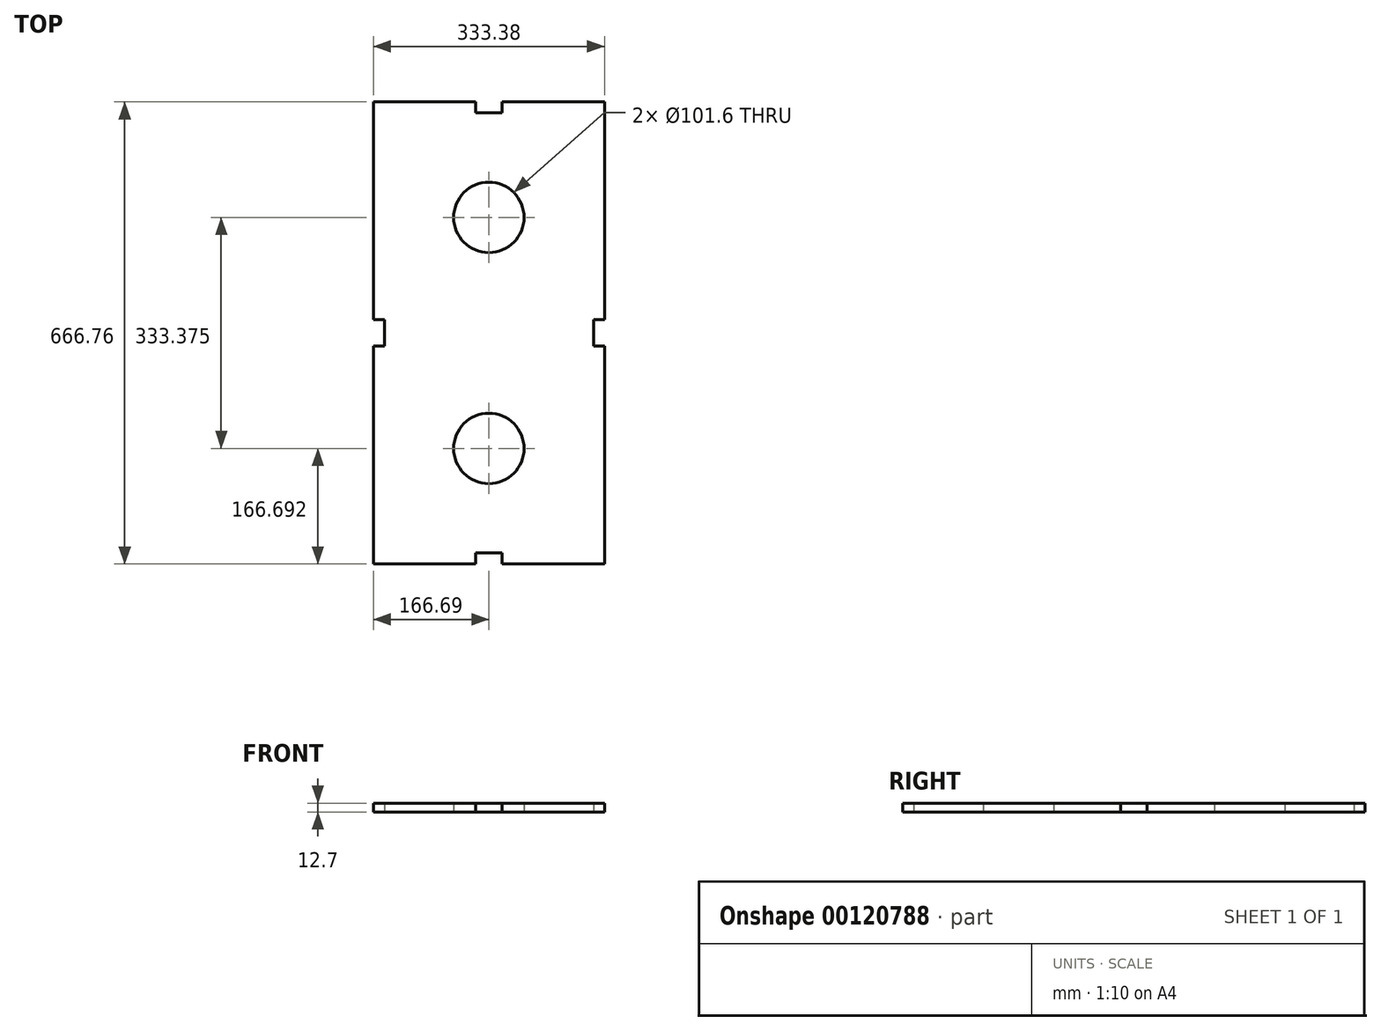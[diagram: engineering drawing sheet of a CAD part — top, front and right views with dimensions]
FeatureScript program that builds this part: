
annotation { "Feature Type Name" : "Feature", "Feature Type Description" : "" }
export const myFeature = defineFeature(function(context is Context, id is Id, definition is map)
    precondition{}
    {
        {
            var Q0;
            Q0=qCreatedBy(makeId("Top.planeOp"),FACE);
            var sketch = newSketch(context, id + "F0", { "sketchPlane" : qUnion([Q0])});
            skLineSegment(sketch, "E0.bottom", {"start": v(166.69, -166.69) * mm, "end": v(-166.69, -166.69) * mm});
            skLineSegment(sketch, "E0.top", {"start": v(166.69, 166.69) * mm, "end": v(-166.69, 166.69) * mm});
            skLineSegment(sketch, "E0.left", {"start": v(166.69, -166.69) * mm, "end": v(166.69, 166.69) * mm});
            skLineSegment(sketch, "E0.right", {"start": v(-166.69, -166.69) * mm, "end": v(-166.69, 166.69) * mm});
            skPoint(sketch, "E0.middle", {"position": v(0, 0) * mm});
            skCircle(sketch, "E1", {"center": v(0, -166.69) * mm, "radius": 50.8 * mm});
            skCircle(sketch, "E2", {"center": v(0, 166.69) * mm, "radius": 50.8 * mm});
            skLineSegment(sketch, "E3.bottom", {"start": v(-166.69, -19.05) * mm, "end": v(-150.81, -19.05) * mm});
            skLineSegment(sketch, "E3.top", {"start": v(-166.69, 19.05) * mm, "end": v(-150.81, 19.05) * mm});
            skLineSegment(sketch, "E3.left", {"start": v(-166.69, -19.05) * mm, "end": v(-166.69, 19.05) * mm});
            skLineSegment(sketch, "E3.right", {"start": v(-150.81, -19.05) * mm, "end": v(-150.81, 19.05) * mm});
            skPoint(sketch, "E3.middle", {"position": v(-158.75, 0) * mm});
            skPoint(sketch, "E3.middle.positionSnap0", {"position": v(-166.69, 0) * mm});
            skPoint(sketch, "E3.centerSnap0", {"position": v(-166.69, 0) * mm});
            skPoint(sketch, "E4.MirrorP", {"position": v(166.69, 0) * mm});
            skLineSegment(sketch, "E5.MirrorCS", {"start": v(166.69, -19.05) * mm, "end": v(150.81, -19.05) * mm});
            skPoint(sketch, "E6.MirrorP", {"position": v(158.75, 0) * mm});
            skLineSegment(sketch, "E7.MirrorCS", {"start": v(150.81, -19.05) * mm, "end": v(150.81, 19.05) * mm});
            skLineSegment(sketch, "E8.MirrorCS", {"start": v(166.69, -19.05) * mm, "end": v(166.69, 19.05) * mm});
            skLineSegment(sketch, "E9.MirrorCS", {"start": v(166.69, 19.05) * mm, "end": v(150.81, 19.05) * mm});
            skLineSegment(sketch, "E10.bottom", {"start": v(19.05, 333.38) * mm, "end": v(-19.05, 333.38) * mm});
            skLineSegment(sketch, "E10.top", {"start": v(19.05, 317.5) * mm, "end": v(-19.05, 317.5) * mm});
            skLineSegment(sketch, "E10.left", {"start": v(19.05, 333.38) * mm, "end": v(19.05, 317.5) * mm});
            skLineSegment(sketch, "E10.right", {"start": v(-19.05, 333.38) * mm, "end": v(-19.05, 317.5) * mm});
            skPoint(sketch, "E10.middle", {"position": v(0, 325.44) * mm});
            skLineSegment(sketch, "E11.MirrorCS", {"start": v(19.05, -333.38) * mm, "end": v(-19.05, -333.38) * mm});
            skLineSegment(sketch, "E12.MirrorCS", {"start": v(19.05, -333.38) * mm, "end": v(19.05, -317.5) * mm});
            skPoint(sketch, "E13.MirrorP", {"position": v(0, -325.44) * mm});
            skLineSegment(sketch, "E14.MirrorCS", {"start": v(-19.05, -333.38) * mm, "end": v(-19.05, -317.5) * mm});
            skLineSegment(sketch, "E15.MirrorCS", {"start": v(19.05, -317.5) * mm, "end": v(-19.05, -317.5) * mm});
            skLineSegment(sketch, "E16.bottom", {"start": v(-166.69, 333.38) * mm, "end": v(166.69, 333.38) * mm});
            skLineSegment(sketch, "E16.top", {"start": v(-166.69, -333.38) * mm, "end": v(166.69, -333.38) * mm});
            skLineSegment(sketch, "E16.left", {"start": v(-166.69, 333.38) * mm, "end": v(-166.69, -333.38) * mm});
            skLineSegment(sketch, "E16.right", {"start": v(166.69, 333.38) * mm, "end": v(166.69, -333.38) * mm});
            skSolve(sketch);
        }
        {
            var Q0;
            {var subQ1=sQuery(id+"F0.wireOp",EDGE,"E0.bottom");var subQ3=sQuery(id+"F0.wireOp",EDGE,"E1");var subQ4=makeQuery(id+"F0.imprint","INTERSECT",VERTEX,{"disambiguationData":[OD(0.0)],"derivedFrom":[subQ1,subQ3]});Q0=makeQuery(id+"F0.imprint","IMPRINT",FACE,{"disambiguationData":[TD([[makeQuery(id+"F0.imprint","IMPRINT",EDGE,{"disambiguationData":[TD([[subQ4,1.0]])],"derivedFrom":subQ3}),-1.0]])]});}
            var Q1;
            {var subQ1=sQuery(id+"F0.wireOp",EDGE,"E0.top");var subQ3=sQuery(id+"F0.wireOp",EDGE,"E2");var subQ4=makeQuery(id+"F0.imprint","INTERSECT",VERTEX,{"disambiguationData":[OD(0.0)],"derivedFrom":[subQ1,subQ3]});Q1=makeQuery(id+"F0.imprint","IMPRINT",FACE,{"disambiguationData":[TD([[makeQuery(id+"F0.imprint","IMPRINT",EDGE,{"disambiguationData":[TD([[subQ4,-1.0]])],"derivedFrom":subQ3}),-1.0]])]});}
            var Q2;
            {var subQ0=sQuery(id+"F0.wireOp",EDGE,"E0.right");Q2=makeQuery(id+"F0.imprint","IMPRINT",FACE,{"disambiguationData":[TD([[makeQuery(id+"F0.imprint","IMPRINT",EDGE,{"derivedFrom":subQ0}),-1.0]])]});}
            var Q3;
            {var subQ1=sQuery(id+"F0.wireOp",EDGE,"E0.bottom");var subQ4=sQuery(id+"F0.wireOp",EDGE,"E1");var subQ7=makeQuery(id+"F0.imprint","INTERSECT",VERTEX,{"disambiguationData":[OD(0.0)],"derivedFrom":[subQ1,subQ4]});Q3=makeQuery(id+"F0.imprint","IMPRINT",FACE,{"disambiguationData":[TD([[makeQuery(id+"F0.imprint","IMPRINT",EDGE,{"disambiguationData":[TD([[subQ7,-1.0]])],"derivedFrom":subQ4}),-1.0]])]});}
            var Q4;
            {var subQ1=sQuery(id+"F0.wireOp",EDGE,"E0.top");var subQ4=sQuery(id+"F0.wireOp",EDGE,"E2");var subQ5=makeQuery(id+"F0.imprint","INTERSECT",VERTEX,{"disambiguationData":[OD(0.0)],"derivedFrom":[subQ1,subQ4]});Q4=makeQuery(id+"F0.imprint","IMPRINT",FACE,{"disambiguationData":[TD([[makeQuery(id+"F0.imprint","IMPRINT",EDGE,{"disambiguationData":[TD([[subQ5,1.0]])],"derivedFrom":subQ4}),-1.0]])]});}
            var Q5;
            {var subQ0=sQuery(id+"F0.wireOp",EDGE,"E0.left");Q5=makeQuery(id+"F0.imprint","IMPRINT",FACE,{"disambiguationData":[TD([[makeQuery(id+"F0.imprint","IMPRINT",EDGE,{"derivedFrom":subQ0}),1.0]])]});}
            extrude(context, id + "F1", {"entities" : qUnion([Q0, Q1, Q2, Q3, Q4, Q5]), "depth" : 12.7 * mm});
        }
    });
